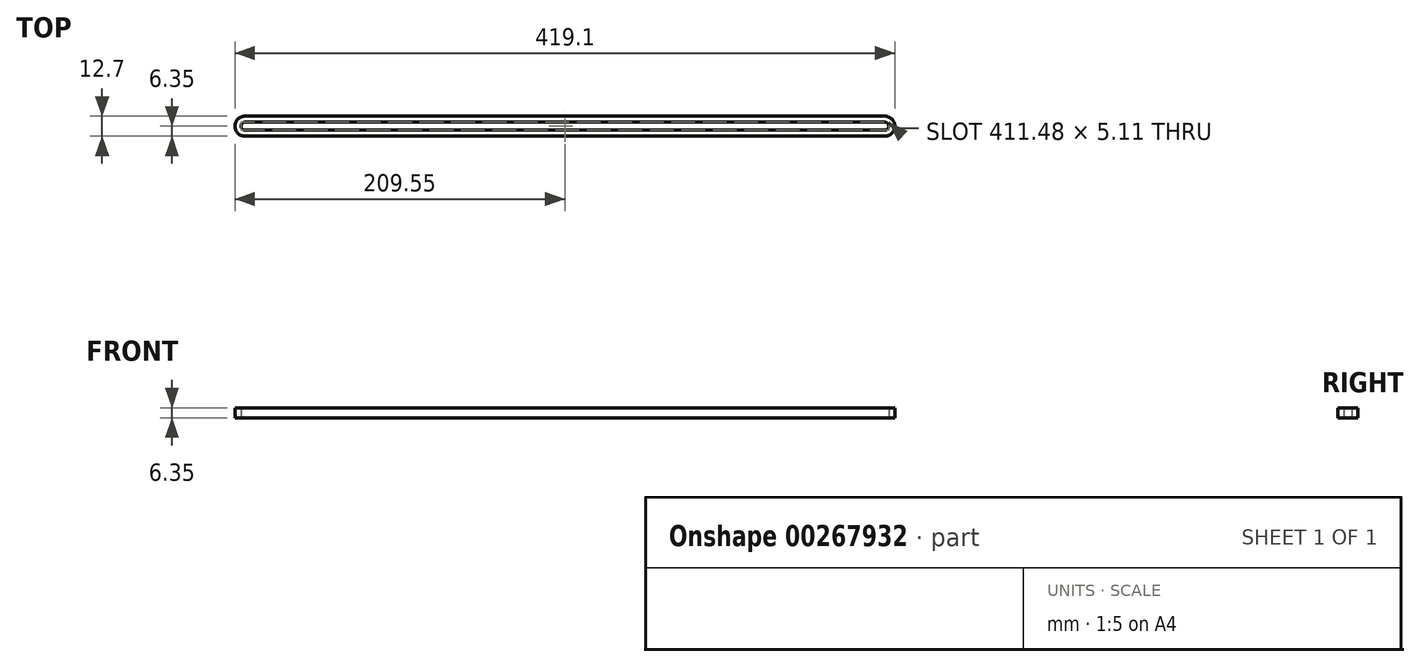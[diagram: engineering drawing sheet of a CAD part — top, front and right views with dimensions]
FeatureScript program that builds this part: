
annotation { "Feature Type Name" : "Feature", "Feature Type Description" : "" }
export const myFeature = defineFeature(function(context is Context, id is Id, definition is map)
    precondition{}
    {
        {
            var Q0;
            Q0=qCreatedBy(makeId("Top.planeOp"),FACE);
            var sketch = newSketch(context, id + "F0", { "sketchPlane" : qUnion([Q0])});
            skLineSegment(sketch, "E0.bottom", {"start": v(-203.19, 2.55) * mm, "end": v(203.19, 2.55) * mm});
            skLineSegment(sketch, "E0.top", {"start": v(-203.19, -2.55) * mm, "end": v(203.19, -2.55) * mm});
            skLineSegment(sketch, "E0.left", {"start": v(-203.19, 2.55) * mm, "end": v(-203.19, -2.55) * mm});
            skLineSegment(sketch, "E0.right", {"start": v(203.19, 2.55) * mm, "end": v(203.19, -2.55) * mm});
            skPoint(sketch, "E0.middle", {"position": v(0, 0) * mm});
            skArc(sketch, "E1", {"start": v(-203.19, 2.55) * mm, "mid": v(-205.74, 0) * mm, "end": v(-203.19, -2.55) * mm});
            skArc(sketch, "E2", {"start": v(203.19, -2.55) * mm, "mid": v(205.74, 0) * mm, "end": v(203.19, 2.55) * mm});
            skLineSegment(sketch, "E3.bottom", {"start": v(-203.2, 6.35) * mm, "end": v(203.2, 6.35) * mm});
            skLineSegment(sketch, "E3.top", {"start": v(-203.2, -6.35) * mm, "end": v(203.2, -6.35) * mm});
            skLineSegment(sketch, "E3.left", {"start": v(-203.2, 6.35) * mm, "end": v(-203.2, -6.35) * mm});
            skLineSegment(sketch, "E3.right", {"start": v(203.2, 6.35) * mm, "end": v(203.2, -6.35) * mm});
            skArc(sketch, "E4", {"start": v(203.2, -6.35) * mm, "mid": v(209.55, 0) * mm, "end": v(203.2, 6.35) * mm});
            skArc(sketch, "E5", {"start": v(-203.2, 6.35) * mm, "mid": v(-209.55, 0) * mm, "end": v(-203.2, -6.35) * mm});
            skLineSegment(sketch, "E6", {"start": v(-205.74, 5.82) * mm, "end": v(-205.74, -5.82) * mm, "construction": true});
            skSolve(sketch);
        }
        {
            var Q0;
            {var subQ4=sQuery(id+"F0.wireOp",EDGE,"E5");Q0=makeQuery(id+"F0.imprint","IMPRINT",FACE,{"disambiguationData":[TD([[makeQuery(id+"F0.imprint","IMPRINT",EDGE,{"derivedFrom":subQ4}),1.0]])]});}
            var Q1;
            {var subQ1=sQuery(id+"F0.wireOp",EDGE,"E0.bottom");Q1=makeQuery(id+"F0.imprint","IMPRINT",FACE,{"disambiguationData":[TD([[makeQuery(id+"F0.imprint","IMPRINT",EDGE,{"derivedFrom":subQ1}),1.0]])]});}
            var Q2;
            {var subQ1=sQuery(id+"F0.wireOp",EDGE,"E0.top");Q2=makeQuery(id+"F0.imprint","IMPRINT",FACE,{"disambiguationData":[TD([[makeQuery(id+"F0.imprint","IMPRINT",EDGE,{"derivedFrom":subQ1}),-1.0]])]});}
            var Q3;
            {var subQ4=sQuery(id+"F0.wireOp",EDGE,"E4");Q3=makeQuery(id+"F0.imprint","IMPRINT",FACE,{"disambiguationData":[TD([[makeQuery(id+"F0.imprint","IMPRINT",EDGE,{"derivedFrom":subQ4}),1.0]])]});}
            extrude(context, id + "F1", {"entities" : qUnion([Q0, Q1, Q2, Q3]), "depth" : 6.35 * mm, "offsetDistance" : 25.4 * mm});
        }
    });
